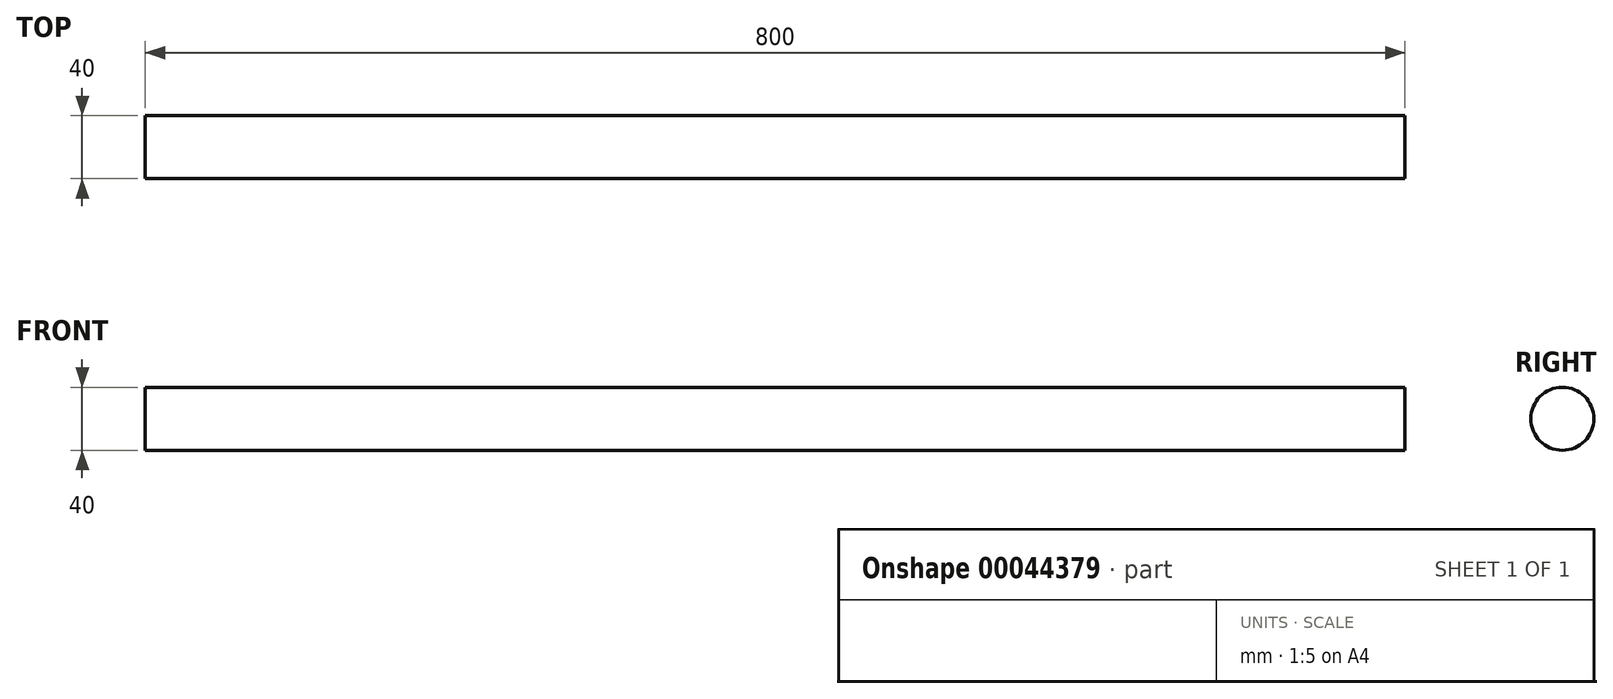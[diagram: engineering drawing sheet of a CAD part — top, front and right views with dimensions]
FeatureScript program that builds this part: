
annotation { "Feature Type Name" : "Feature", "Feature Type Description" : "" }
export const myFeature = defineFeature(function(context is Context, id is Id, definition is map)
    precondition{}
    {
        {
            var Q0;
            Q0=qCreatedBy(makeId("Right.planeOp"),FACE);
            var sketch = newSketch(context, id + "F0", { "sketchPlane" : qUnion([Q0])});
            skCircle(sketch, "E0", {"center": v(0, 0) * mm, "radius": 20 * mm});
            skSolve(sketch);
        }
        {
            var Q0;
            Q0 = qSketchRegion(id + "F0", true);
            extrude(context, id + "F1", {"entities" : qUnion([Q0]), "depth" : 800 * mm});
        }
    });
